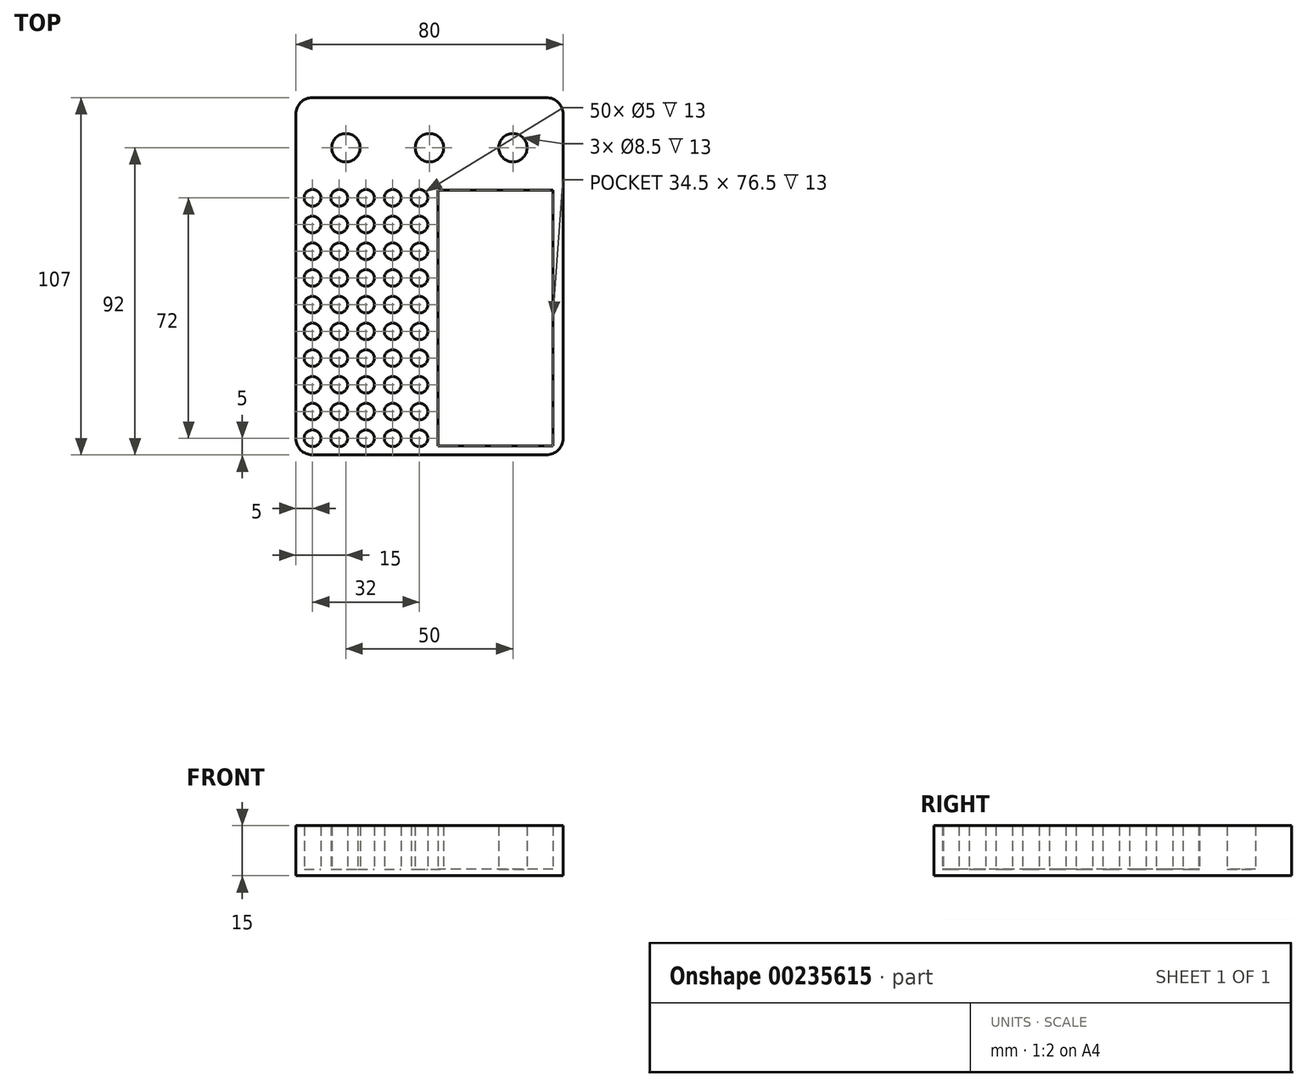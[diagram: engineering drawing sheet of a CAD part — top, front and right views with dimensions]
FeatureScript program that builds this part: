
annotation { "Feature Type Name" : "Feature", "Feature Type Description" : "" }
export const myFeature = defineFeature(function(context is Context, id is Id, definition is map)
    precondition{}
    {
        {
            var Q0;
            Q0=qCreatedBy(makeId("Top.planeOp"),FACE);
            var sketch = newSketch(context, id + "F0", { "sketchPlane" : qUnion([Q0])});
            skLineSegment(sketch, "E0.bottom", {"start": v(0, 0) * mm, "end": v(80, 0) * mm});
            skLineSegment(sketch, "E0.top", {"start": v(0, 107) * mm, "end": v(80, 107) * mm});
            skLineSegment(sketch, "E0.left", {"start": v(0, 0) * mm, "end": v(0, 107) * mm});
            skLineSegment(sketch, "E0.right", {"start": v(80, 0) * mm, "end": v(80, 107) * mm});
            skCircle(sketch, "E1", {"center": v(5, 5) * mm, "radius": 2.5 * mm});
            skCircle(sketch, "E2.0.1.0", {"center": v(5, 13) * mm, "radius": 2.5 * mm});
            skCircle(sketch, "E2.0.2.0", {"center": v(5, 21) * mm, "radius": 2.5 * mm});
            skCircle(sketch, "E2.0.3.0", {"center": v(5, 29) * mm, "radius": 2.5 * mm});
            skCircle(sketch, "E2.0.4.0", {"center": v(5, 37) * mm, "radius": 2.5 * mm});
            skCircle(sketch, "E2.0.5.0", {"center": v(5, 45) * mm, "radius": 2.5 * mm});
            skCircle(sketch, "E2.0.6.0", {"center": v(5, 53) * mm, "radius": 2.5 * mm});
            skCircle(sketch, "E2.0.7.0", {"center": v(5, 61) * mm, "radius": 2.5 * mm});
            skCircle(sketch, "E2.0.8.0", {"center": v(5, 69) * mm, "radius": 2.5 * mm});
            skCircle(sketch, "E2.0.9.0", {"center": v(5, 77) * mm, "radius": 2.5 * mm});
            skCircle(sketch, "E2.1.0.0", {"center": v(13, 5) * mm, "radius": 2.5 * mm});
            skCircle(sketch, "E2.1.1.0", {"center": v(13, 13) * mm, "radius": 2.5 * mm});
            skCircle(sketch, "E2.1.2.0", {"center": v(13, 21) * mm, "radius": 2.5 * mm});
            skCircle(sketch, "E2.1.3.0", {"center": v(13, 29) * mm, "radius": 2.5 * mm});
            skCircle(sketch, "E2.1.4.0", {"center": v(13, 37) * mm, "radius": 2.5 * mm});
            skCircle(sketch, "E2.1.5.0", {"center": v(13, 45) * mm, "radius": 2.5 * mm});
            skCircle(sketch, "E2.1.6.0", {"center": v(13, 53) * mm, "radius": 2.5 * mm});
            skCircle(sketch, "E2.1.7.0", {"center": v(13, 61) * mm, "radius": 2.5 * mm});
            skCircle(sketch, "E2.1.8.0", {"center": v(13, 69) * mm, "radius": 2.5 * mm});
            skCircle(sketch, "E2.1.9.0", {"center": v(13, 77) * mm, "radius": 2.5 * mm});
            skCircle(sketch, "E2.2.0.0", {"center": v(21, 5) * mm, "radius": 2.5 * mm});
            skCircle(sketch, "E2.2.1.0", {"center": v(21, 13) * mm, "radius": 2.5 * mm});
            skCircle(sketch, "E2.2.2.0", {"center": v(21, 21) * mm, "radius": 2.5 * mm});
            skCircle(sketch, "E2.2.3.0", {"center": v(21, 29) * mm, "radius": 2.5 * mm});
            skCircle(sketch, "E2.2.4.0", {"center": v(21, 37) * mm, "radius": 2.5 * mm});
            skCircle(sketch, "E2.2.5.0", {"center": v(21, 45) * mm, "radius": 2.5 * mm});
            skCircle(sketch, "E2.2.6.0", {"center": v(21, 53) * mm, "radius": 2.5 * mm});
            skCircle(sketch, "E2.2.7.0", {"center": v(21, 61) * mm, "radius": 2.5 * mm});
            skCircle(sketch, "E2.2.8.0", {"center": v(21, 69) * mm, "radius": 2.5 * mm});
            skCircle(sketch, "E2.2.9.0", {"center": v(21, 77) * mm, "radius": 2.5 * mm});
            skCircle(sketch, "E2.3.0.0", {"center": v(29, 5) * mm, "radius": 2.5 * mm});
            skCircle(sketch, "E2.3.1.0", {"center": v(29, 13) * mm, "radius": 2.5 * mm});
            skCircle(sketch, "E2.3.2.0", {"center": v(29, 21) * mm, "radius": 2.5 * mm});
            skCircle(sketch, "E2.3.3.0", {"center": v(29, 29) * mm, "radius": 2.5 * mm});
            skCircle(sketch, "E2.3.4.0", {"center": v(29, 37) * mm, "radius": 2.5 * mm});
            skCircle(sketch, "E2.3.5.0", {"center": v(29, 45) * mm, "radius": 2.5 * mm});
            skCircle(sketch, "E2.3.6.0", {"center": v(29, 53) * mm, "radius": 2.5 * mm});
            skCircle(sketch, "E2.3.7.0", {"center": v(29, 61) * mm, "radius": 2.5 * mm});
            skCircle(sketch, "E2.3.8.0", {"center": v(29, 69) * mm, "radius": 2.5 * mm});
            skCircle(sketch, "E2.3.9.0", {"center": v(29, 77) * mm, "radius": 2.5 * mm});
            skCircle(sketch, "E2.4.0.0", {"center": v(37, 5) * mm, "radius": 2.5 * mm});
            skCircle(sketch, "E2.4.1.0", {"center": v(37, 13) * mm, "radius": 2.5 * mm});
            skCircle(sketch, "E2.4.2.0", {"center": v(37, 21) * mm, "radius": 2.5 * mm});
            skCircle(sketch, "E2.4.3.0", {"center": v(37, 29) * mm, "radius": 2.5 * mm});
            skCircle(sketch, "E2.4.4.0", {"center": v(37, 37) * mm, "radius": 2.5 * mm});
            skCircle(sketch, "E2.4.5.0", {"center": v(37, 45) * mm, "radius": 2.5 * mm});
            skCircle(sketch, "E2.4.6.0", {"center": v(37, 53) * mm, "radius": 2.5 * mm});
            skCircle(sketch, "E2.4.7.0", {"center": v(37, 61) * mm, "radius": 2.5 * mm});
            skCircle(sketch, "E2.4.8.0", {"center": v(37, 69) * mm, "radius": 2.5 * mm});
            skCircle(sketch, "E2.4.9.0", {"center": v(37, 77) * mm, "radius": 2.5 * mm});
            skLineSegment(sketch, "E2.direction1", {"start": v(5, 5) * mm, "end": v(13, 5) * mm, "construction": true});
            skLineSegment(sketch, "E2.direction2", {"start": v(5, 5) * mm, "end": v(5, 13) * mm, "construction": true});
            skCircle(sketch, "E3", {"center": v(15, 92) * mm, "radius": 4.25 * mm});
            skCircle(sketch, "E4", {"center": v(40, 92) * mm, "radius": 4.25 * mm});
            skCircle(sketch, "E5", {"center": v(65, 92) * mm, "radius": 4.25 * mm});
            skLineSegment(sketch, "E6.bottom", {"start": v(42.5, 2.75) * mm, "end": v(77, 2.75) * mm});
            skLineSegment(sketch, "E6.top", {"start": v(42.5, 79.25) * mm, "end": v(77, 79.25) * mm});
            skLineSegment(sketch, "E6.left", {"start": v(42.5, 2.75) * mm, "end": v(42.5, 79.25) * mm});
            skLineSegment(sketch, "E6.right", {"start": v(77, 2.75) * mm, "end": v(77, 79.25) * mm});
            skSolve(sketch);
        }
        {
            var Q0;
            Q0 = qSketchRegion(id + "F0", true);
            extrude(context, id + "F1", {"entities" : qUnion([Q0]), "depth" : 15 * mm, "offsetDistance" : 25 * mm});
        }
        {
            var Q0;
            Q0=makeQuery(id+"F1.opExtrude","CAP_FACE",FACE,{"disambiguationData":[OSD([sQuery(id+"F0.wireOp",EDGE,"E0.bottom"),sQuery(id+"F0.wireOp",EDGE,"E0.top"),sQuery(id+"F0.wireOp",EDGE,"E0.left"),sQuery(id+"F0.wireOp",EDGE,"E0.right"),sQuery(id+"F0.wireOp",EDGE,"E1"),sQuery(id+"F0.wireOp",EDGE,"E2.0.1.0"),sQuery(id+"F0.wireOp",EDGE,"E2.0.2.0"),sQuery(id+"F0.wireOp",EDGE,"E2.0.3.0"),sQuery(id+"F0.wireOp",EDGE,"E2.0.4.0"),sQuery(id+"F0.wireOp",EDGE,"E2.0.5.0"),sQuery(id+"F0.wireOp",EDGE,"E2.0.6.0"),sQuery(id+"F0.wireOp",EDGE,"E2.0.7.0"),sQuery(id+"F0.wireOp",EDGE,"E2.0.8.0"),sQuery(id+"F0.wireOp",EDGE,"E2.0.9.0"),sQuery(id+"F0.wireOp",EDGE,"E2.1.0.0"),sQuery(id+"F0.wireOp",EDGE,"E2.1.1.0"),sQuery(id+"F0.wireOp",EDGE,"E2.1.2.0"),sQuery(id+"F0.wireOp",EDGE,"E2.1.3.0"),sQuery(id+"F0.wireOp",EDGE,"E2.1.4.0"),sQuery(id+"F0.wireOp",EDGE,"E2.1.5.0"),sQuery(id+"F0.wireOp",EDGE,"E2.1.6.0"),sQuery(id+"F0.wireOp",EDGE,"E2.1.7.0"),sQuery(id+"F0.wireOp",EDGE,"E2.1.8.0"),sQuery(id+"F0.wireOp",EDGE,"E2.1.9.0"),sQuery(id+"F0.wireOp",EDGE,"E2.2.0.0"),sQuery(id+"F0.wireOp",EDGE,"E2.2.1.0"),sQuery(id+"F0.wireOp",EDGE,"E2.2.2.0"),sQuery(id+"F0.wireOp",EDGE,"E2.2.3.0"),sQuery(id+"F0.wireOp",EDGE,"E2.2.4.0"),sQuery(id+"F0.wireOp",EDGE,"E2.2.5.0"),sQuery(id+"F0.wireOp",EDGE,"E2.2.6.0"),sQuery(id+"F0.wireOp",EDGE,"E2.2.7.0"),sQuery(id+"F0.wireOp",EDGE,"E2.2.8.0"),sQuery(id+"F0.wireOp",EDGE,"E2.2.9.0"),sQuery(id+"F0.wireOp",EDGE,"E2.3.0.0"),sQuery(id+"F0.wireOp",EDGE,"E2.3.1.0"),sQuery(id+"F0.wireOp",EDGE,"E2.3.2.0"),sQuery(id+"F0.wireOp",EDGE,"E2.3.3.0"),sQuery(id+"F0.wireOp",EDGE,"E2.3.4.0"),sQuery(id+"F0.wireOp",EDGE,"E2.3.5.0"),sQuery(id+"F0.wireOp",EDGE,"E2.3.6.0"),sQuery(id+"F0.wireOp",EDGE,"E2.3.7.0"),sQuery(id+"F0.wireOp",EDGE,"E2.3.8.0"),sQuery(id+"F0.wireOp",EDGE,"E2.3.9.0"),sQuery(id+"F0.wireOp",EDGE,"E2.4.0.0"),sQuery(id+"F0.wireOp",EDGE,"E2.4.1.0"),sQuery(id+"F0.wireOp",EDGE,"E2.4.2.0"),sQuery(id+"F0.wireOp",EDGE,"E2.4.3.0"),sQuery(id+"F0.wireOp",EDGE,"E2.4.4.0"),sQuery(id+"F0.wireOp",EDGE,"E2.4.5.0"),sQuery(id+"F0.wireOp",EDGE,"E2.4.6.0"),sQuery(id+"F0.wireOp",EDGE,"E2.4.7.0"),sQuery(id+"F0.wireOp",EDGE,"E2.4.8.0"),sQuery(id+"F0.wireOp",EDGE,"E2.4.9.0"),sQuery(id+"F0.wireOp",EDGE,"E3"),sQuery(id+"F0.wireOp",EDGE,"E4"),sQuery(id+"F0.wireOp",EDGE,"E5"),sQuery(id+"F0.wireOp",EDGE,"E6.bottom"),sQuery(id+"F0.wireOp",EDGE,"E6.top"),sQuery(id+"F0.wireOp",EDGE,"E6.left"),sQuery(id+"F0.wireOp",EDGE,"E6.right")])],"isStart":true});
            var sketch = newSketch(context, id + "F2", { "sketchPlane" : qUnion([Q0])});
            skLineSegment(sketch, "E7.bottom", {"start": v(80, -107) * mm, "end": v(0, -107) * mm});
            skLineSegment(sketch, "E7.top", {"start": v(80, 0) * mm, "end": v(0, 0) * mm});
            skLineSegment(sketch, "E7.left", {"start": v(80, -107) * mm, "end": v(80, 0) * mm});
            skLineSegment(sketch, "E7.right", {"start": v(0, -107) * mm, "end": v(0, 0) * mm});
            skSolve(sketch);
        }
        {
            var Q0;
            Q0 = qSketchRegion(id + "F2", true);
            extrude(context, id + "F3", {"entities" : qUnion([Q0]), "operationType" : NewBodyOperationType.ADD, "oppositeDirection" : true, "depth" : 2 * mm, "offsetDistance" : 25 * mm});
        }
        {
            var Q0;
            Q0=makeQuery(id+"F1.opExtrude","SWEPT_EDGE",EDGE,{"disambiguationData":[OSD([sQuery(id+"F0.wireOp",EDGE,"E0.top"),sQuery(id+"F0.wireOp",EDGE,"E0.left")])]});
            var Q1;
            Q1=makeQuery(id+"F1.opExtrude","SWEPT_EDGE",EDGE,{"disambiguationData":[OSD([sQuery(id+"F0.wireOp",EDGE,"E0.bottom"),sQuery(id+"F0.wireOp",EDGE,"E0.left")])]});
            var Q2;
            Q2=makeQuery(id+"F1.opExtrude","SWEPT_EDGE",EDGE,{"disambiguationData":[OSD([sQuery(id+"F0.wireOp",EDGE,"E0.bottom"),sQuery(id+"F0.wireOp",EDGE,"E0.right")])]});
            var Q3;
            Q3=makeQuery(id+"F1.opExtrude","SWEPT_EDGE",EDGE,{"disambiguationData":[OSD([sQuery(id+"F0.wireOp",EDGE,"E0.top"),sQuery(id+"F0.wireOp",EDGE,"E0.right")])]});
            fillet(context, id + "F4", {"entities" : qUnion([Q0, Q1, Q2, Q3]), "radius" : 5 * mm, "tangentPropagation" : true, "allowEdgeOverflow" : false});
        }
    });
